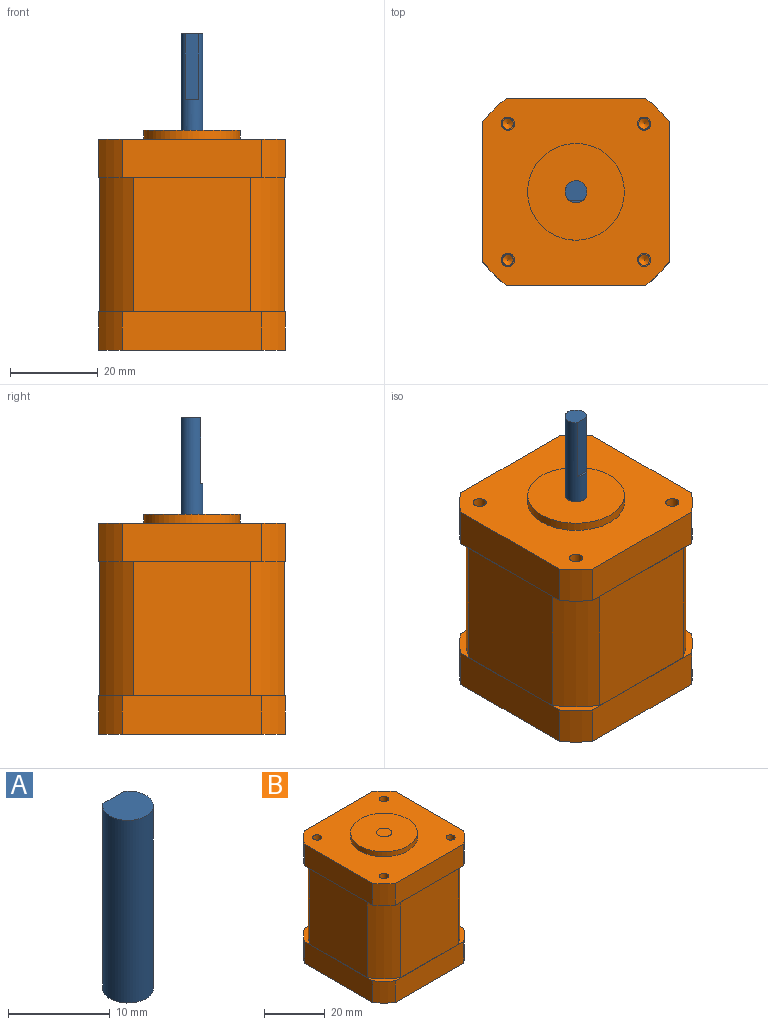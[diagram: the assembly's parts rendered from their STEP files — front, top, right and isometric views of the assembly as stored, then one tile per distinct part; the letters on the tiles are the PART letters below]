
ASSEMBLY  parts=2 mates=1
PART A: 5 faces, bbox 5x5x22 mm
  f0: plane 3x0.5mm, normal (0,0,1), area 1mm2, adj f1,f3
  f1: plane 15x3mm, normal (0,1,0), area 45mm2, adj f0,f2,f3
  f2: plane 5x4.5mm, normal (0,0,1), area 18.6mm2, adj f1,f3
  f3: cylinder r=2.5mm len=22mm, axis (0,0,-1), area 297.3mm2, adj f0,f1,f2,f4
  f4: plane 5x5mm, normal (0,0,-1), area 19.6mm2, adj f3
PART B: 47 faces, bbox 42.4x42.4x50 mm
  f0: cylinder r=1.5mm len=6mm, axis (0,0,1), area 56.5mm2, adj f18,f26
  f1: cylinder r=1.25mm len=2.5mm, axis (0,0,1), area 11.8mm2, adj f2,f26
  f2: cone r=1.25mm half-angle=59deg, axis (0,0,1), area 5.7mm2, adj f1
  f3: cylinder r=1.5mm len=6mm, axis (0,0,1), area 56.5mm2, adj f18,f25
  f4: cylinder r=1.25mm len=2.5mm, axis (0,0,1), area 11.8mm2, adj f5,f25
  f5: cone r=1.25mm half-angle=59deg, axis (0,0,1), area 5.7mm2, adj f4
  f6: cylinder r=1.5mm len=6mm, axis (0,0,1), area 56.5mm2, adj f18,f24
  f7: cylinder r=1.25mm len=2.5mm, axis (0,0,1), area 11.8mm2, adj f8,f24
  f8: cone r=1.25mm half-angle=59deg, axis (0,0,1), area 5.7mm2, adj f7
  f9: cylinder r=1.5mm len=6mm, axis (0,0,1), area 56.5mm2, adj f18,f23
  f10: cylinder r=1.25mm len=2.5mm, axis (0,0,1), area 11.8mm2, adj f11,f23
  f11: cone r=1.25mm half-angle=59deg, axis (0,0,1), area 5.7mm2, adj f10
  f12: cylinder r=11mm len=22mm, axis (0,0,-1), area 138.2mm2, adj f13,f18
  f13: plane 22x22mm, normal (0,0,1), area 360.5mm2, adj f12,f46
  f14: plane 31.78x8.75mm, normal (1,0,0), area 278mm2, adj f18,f19,f20,f28
  f15: plane 31.78x8.75mm, normal (0,-1,0), area 278mm2, adj f18,f19,f21,f28
  f16: plane 31.78x8.75mm, normal (-1,0,0), area 278mm2, adj f18,f21,f22,f28
  f17: plane 31.78x8.75mm, normal (0,1,0), area 278mm2, adj f18,f20,f22,f28
  f18: plane 42.42x42.42mm, normal (0,0,1), area 1339.6mm2, adj f0,f3,f6,f9,f12,f14,f15,f16
  f19: cylinder r=26.5mm len=8.75mm, axis (0,0,-1), area 66.1mm2, adj f14,f15,f18,f28
  f20: cylinder r=26.5mm len=8.75mm, axis (0,0,-1), area 66.1mm2, adj f14,f17,f18,f28
  f21: cylinder r=26.5mm len=8.75mm, axis (0,0,-1), area 66.1mm2, adj f15,f16,f18,f28
  f22: cylinder r=26.5mm len=8.75mm, axis (0,0,-1), area 66.1mm2, adj f16,f17,f18,f28
  f23: plane 3x3mm, normal (0,0,1), area 2.2mm2, adj f9,f10
  f24: plane 3x3mm, normal (0,0,1), area 2.2mm2, adj f6,f7
  f25: plane 3x3mm, normal (0,0,1), area 2.2mm2, adj f3,f4
  f26: plane 3x3mm, normal (0,0,1), area 2.2mm2, adj f0,f1
  f27: plane 42.42x42.42mm, normal (0,0,1), area 67.2mm2, adj f29,f30,f31,f32,f33,f34,f35,f36
  f28: plane 42.42x42.42mm, normal (0,0,-1), area 67.2mm2, adj f14,f15,f16,f17,f19,f20,f21,f22
  f29: cylinder r=25mm len=30.5mm, axis (0,0,1), area 335.5mm2, adj f27,f28,f30,f36
  f30: plane 30.5x26.79mm, normal (0,1,0), area 817.1mm2, adj f27,f28,f29,f31
  f31: cylinder r=25mm len=30.5mm, axis (0,0,1), area 335.5mm2, adj f27,f28,f30,f32
  f32: plane 30.5x26.79mm, normal (1,0,0), area 817.1mm2, adj f27,f28,f31,f33
  f33: cylinder r=25mm len=30.5mm, axis (0,0,1), area 335.5mm2, adj f27,f28,f32,f34
  f34: plane 30.5x26.79mm, normal (0,-1,0), area 817.1mm2, adj f27,f28,f33,f35
  f35: cylinder r=25mm len=30.5mm, axis (0,0,1), area 335.5mm2, adj f27,f28,f34,f36
  f36: plane 30.5x26.79mm, normal (-1,0,0), area 817.1mm2, adj f27,f28,f29,f35
  f37: plane 42.42x42.42mm, normal (0,0,-1), area 1748.1mm2, adj f38,f39,f40,f41,f42,f43,f44,f45
  f38: cylinder r=26.5mm len=8.75mm, axis (0,0,-1), area 66.1mm2, adj f27,f37,f44,f45
  f39: cylinder r=26.5mm len=8.75mm, axis (0,0,-1), area 66.1mm2, adj f27,f37,f43,f44
  f40: cylinder r=26.5mm len=8.75mm, axis (0,0,-1), area 66.1mm2, adj f27,f37,f42,f43
  f41: cylinder r=26.5mm len=8.75mm, axis (0,0,-1), area 66.1mm2, adj f27,f37,f42,f45
  f42: plane 31.78x8.75mm, normal (0,1,0), area 278mm2, adj f27,f37,f40,f41
  f43: plane 31.78x8.75mm, normal (-1,0,0), area 278mm2, adj f27,f37,f39,f40
  f44: plane 31.78x8.75mm, normal (0,-1,0), area 278mm2, adj f27,f37,f38,f39
  f45: plane 31.78x8.75mm, normal (1,0,0), area 278mm2, adj f27,f37,f38,f41
  f46: plane 5x5mm, normal (0,0,1), area 19.6mm2, adj f13
PLACE A rot(axis=(0,0,1),180deg) t=(-1.16,-11.44,-21.75)mm
PLACE B t=(-1.16,-11.44,-21.75)mm
MATE revolute A.f3 <-> B.f12  axis (0,0,-1) through (-1.16,-11.44,-19.75)mm
